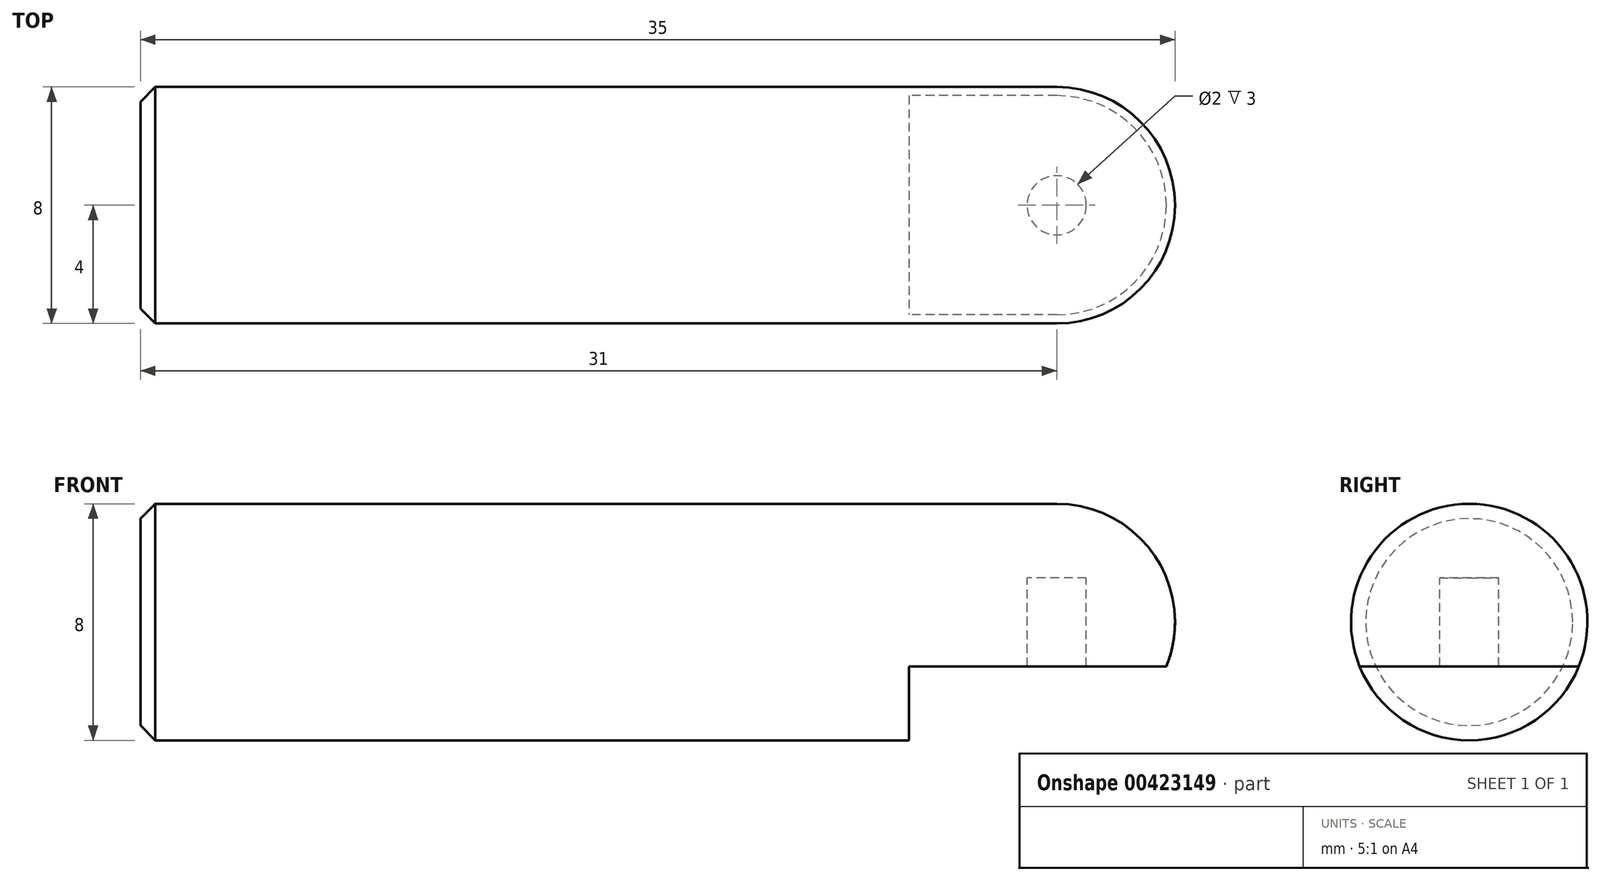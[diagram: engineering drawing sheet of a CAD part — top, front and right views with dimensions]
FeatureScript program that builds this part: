
annotation { "Feature Type Name" : "Feature", "Feature Type Description" : "" }
export const myFeature = defineFeature(function(context is Context, id is Id, definition is map)
    precondition{}
    {
        {
            var Q0;
            Q0=qCreatedBy(makeId("Front.planeOp"),FACE);
            var sketch = newSketch(context, id + "F0", { "sketchPlane" : qUnion([Q0])});
            skLineSegment(sketch, "E0", {"start": v(0, 0) * mm, "end": v(45.95, 0) * mm, "construction": true});
            skLineSegment(sketch, "E1", {"start": v(0, 0) * mm, "end": v(0, 4) * mm});
            skLineSegment(sketch, "E2", {"start": v(0, 4) * mm, "end": v(31, 4) * mm});
            skLineSegment(sketch, "E3", {"start": v(31, 4) * mm, "end": v(31, 4) * mm});
            skLineSegment(sketch, "E4", {"start": v(35, 0) * mm, "end": v(35, 0) * mm});
            skLineSegment(sketch, "E5", {"start": v(35, 0) * mm, "end": v(0, 0) * mm});
            skPoint(sketch, "E6.visualSharp", {"position": v(35, 4) * mm});
            skArc(sketch, "E6.filletArc", {"start": v(35, 0) * mm, "mid": v(33.83, 2.83) * mm, "end": v(31, 4) * mm});
            skSolve(sketch);
        }
        {
            var Q0;
            Q0=makeQuery(id+"F0.imprint","IMPRINT",FACE,{"disambiguationData":[TD([[makeQuery(id+"F0.imprint","IMPRINT",EDGE,{"derivedFrom":sQuery(id+"F0.wireOp",EDGE,"E1")}),-1.0]])]});
            var Q1;
            Q1 = qConstructionFilter(qBodyType(qCreatedBy(id + "F0" ,EDGE), BodyType.WIRE), ConstructionObject.NO);
            var Q2;
            Q2=sQuery(id+"F0.wireOp",EDGE,"E0");
            revolve(context, id + "F1", {"entities" : qUnion([Q0]), "surfaceEntities" : qUnion([Q1]), "axis" : qUnion([Q2]), "revolveType" : RevolveType.FULL});
        }
        {
            var Q0;
            Q0=makeQuery(id+"F1.opRevolve","SWEPT_EDGE",EDGE,{"disambiguationData":[OSD([sQuery(id+"F0.wireOp",EDGE,"E1"),sQuery(id+"F0.wireOp",EDGE,"E2")])]});
            chamfer(context, id + "F2", {"entities" : qUnion([Q0]), "width" : 0.5 * mm, "tangentPropagation" : true});
        }
        {
            var Q0;
            Q0=qCreatedBy(makeId("Top.planeOp"),FACE);
            var sketch = newSketch(context, id + "F3", { "sketchPlane" : qUnion([Q0])});
            skArc(sketch, "E7", {"start": v(31, -4) * mm, "mid": v(35, 0) * mm, "end": v(31, 4) * mm});
            skLineSegment(sketch, "E8", {"start": v(26, 4) * mm, "end": v(31, 4) * mm});
            skLineSegment(sketch, "E9", {"start": v(31, -4) * mm, "end": v(26, -4) * mm});
            skLineSegment(sketch, "E10", {"start": v(26, 4) * mm, "end": v(26, -4) * mm});
            skSolve(sketch);
        }
        {
            var Q0;
            Q0 = qSketchRegion(id + "F3", true);
            extrude(context, id + "F4", {"entities" : qUnion([Q0]), "operationType" : NewBodyOperationType.REMOVE, "oppositeDirection" : true, "depth" : 8 * mm, "hasSecondDirection" : true, "secondDirectionOppositeDirection" : false, "secondDirectionDepth" : -1.5 * mm});
        }
        {
            var Q0;
            Q0=qCreatedBy(makeId("Top.planeOp"),FACE);
            var sketch = newSketch(context, id + "F5", { "sketchPlane" : qUnion([Q0])});
            skArc(sketch, "E11", {"start": v(31, -4) * mm, "mid": v(35, 0) * mm, "end": v(31, 4) * mm});
            skCircle(sketch, "E12", {"center": v(31, 0) * mm, "radius": 1 * mm});
            skSolve(sketch);
        }
        {
            var Q0;
            Q0 = qSketchRegion(id + "F5", true);
            extrude(context, id + "F6", {"entities" : qUnion([Q0]), "operationType" : NewBodyOperationType.REMOVE, "oppositeDirection" : true, "depth" : 3 * mm, "hasSecondDirection" : true, "secondDirectionOppositeDirection" : false, "secondDirectionDepth" : 25 * mm, "symmetric" : true});
        }
    });
